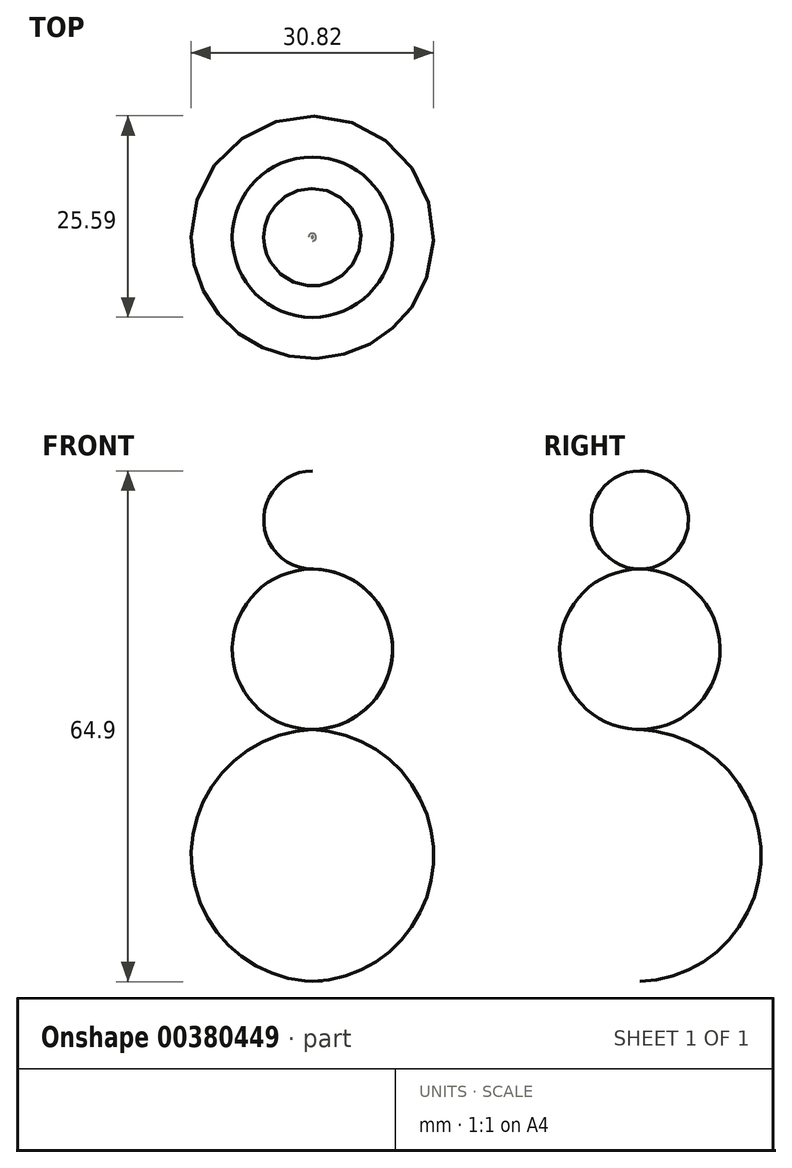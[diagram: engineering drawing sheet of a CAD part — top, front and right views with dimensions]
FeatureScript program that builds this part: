
annotation { "Feature Type Name" : "Feature", "Feature Type Description" : "" }
export const myFeature = defineFeature(function(context is Context, id is Id, definition is map)
    precondition{}
    {
        {
            var Q0;
            Q0=qCreatedBy(makeId("Front.planeOp"),FACE);
            var sketch = newSketch(context, id + "F0", { "sketchPlane" : qUnion([Q0])});
            skLineSegment(sketch, "E0", {"start": v(0, 0) * mm, "end": v(0, -32.03) * mm});
            skLineSegment(sketch, "E1", {"start": v(0, 0) * mm, "end": v(0, 20.37) * mm});
            skLineSegment(sketch, "E2", {"start": v(0, 20.37) * mm, "end": v(0, 32.86) * mm});
            skArc(sketch, "E3", {"start": v(0, 20.37) * mm, "mid": v(6.3, 26.61) * mm, "end": v(0, 32.86) * mm});
            skArc(sketch, "E4", {"start": v(0, 0) * mm, "mid": v(10.18, 10.18) * mm, "end": v(0, 20.37) * mm});
            skArc(sketch, "E5", {"start": v(0, -32.03) * mm, "mid": v(16.65, -16.02) * mm, "end": v(0, 0) * mm});
            skSolve(sketch);
        }
        {
            var Q0;
            {var subQ0=sQuery(id+"F0.wireOp",EDGE,"E2");Q0=makeQuery(id+"F0.imprint","IMPRINT",FACE,{"disambiguationData":[TD([[makeQuery(id+"F0.imprint","IMPRINT",EDGE,{"derivedFrom":subQ0}),-1.0]])]});}
            var Q1;
            {var subQ0=sQuery(id+"F0.wireOp",EDGE,"E1");Q1=makeQuery(id+"F0.imprint","IMPRINT",FACE,{"disambiguationData":[TD([[makeQuery(id+"F0.imprint","IMPRINT",EDGE,{"derivedFrom":subQ0}),-1.0]])]});}
            var Q2;
            {var subQ0=sQuery(id+"F0.wireOp",EDGE,"E0");Q2=makeQuery(id+"F0.imprint","IMPRINT",FACE,{"disambiguationData":[TD([[makeQuery(id+"F0.imprint","IMPRINT",EDGE,{"derivedFrom":subQ0}),1.0]])]});}
            var Q3;
            Q3=sQuery(id+"F0.wireOp",EDGE,"E0");
            revolve(context, id + "F1", {"entities" : qUnion([Q0, Q1, Q2]), "axis" : qUnion([Q3]), "revolveType" : RevolveType.FULL});
        }
        {
            var Q0;
            Q0=qCreatedBy(makeId("Front.planeOp"),FACE);
            var sketch = newSketch(context, id + "F2", { "sketchPlane" : qUnion([Q0])});
            skCircle(sketch, "E6", {"center": v(-2.8, 28.86) * mm, "radius": 1.06 * mm});
            skCircle(sketch, "E7", {"center": v(2.72, 28.86) * mm, "radius": 1.29 * mm});
            skArc(sketch, "E8", {"start": v(-3.6, 24.68) * mm, "mid": v(-0.16, 22.56) * mm, "end": v(3.28, 24.68) * mm});
            skLineSegment(sketch, "E9", {"start": v(-3.6, 24.68) * mm, "end": v(3.28, 24.68) * mm});
            skSolve(sketch);
        }
        {
            var Q0;
            Q0 = qSketchRegion(id + "F2", true);
            extrude(context, id + "F3", {"entities" : qUnion([Q0]), "operationType" : NewBodyOperationType.REMOVE, "oppositeDirection" : true, "depth" : 25.4 * mm});
        }
    });
